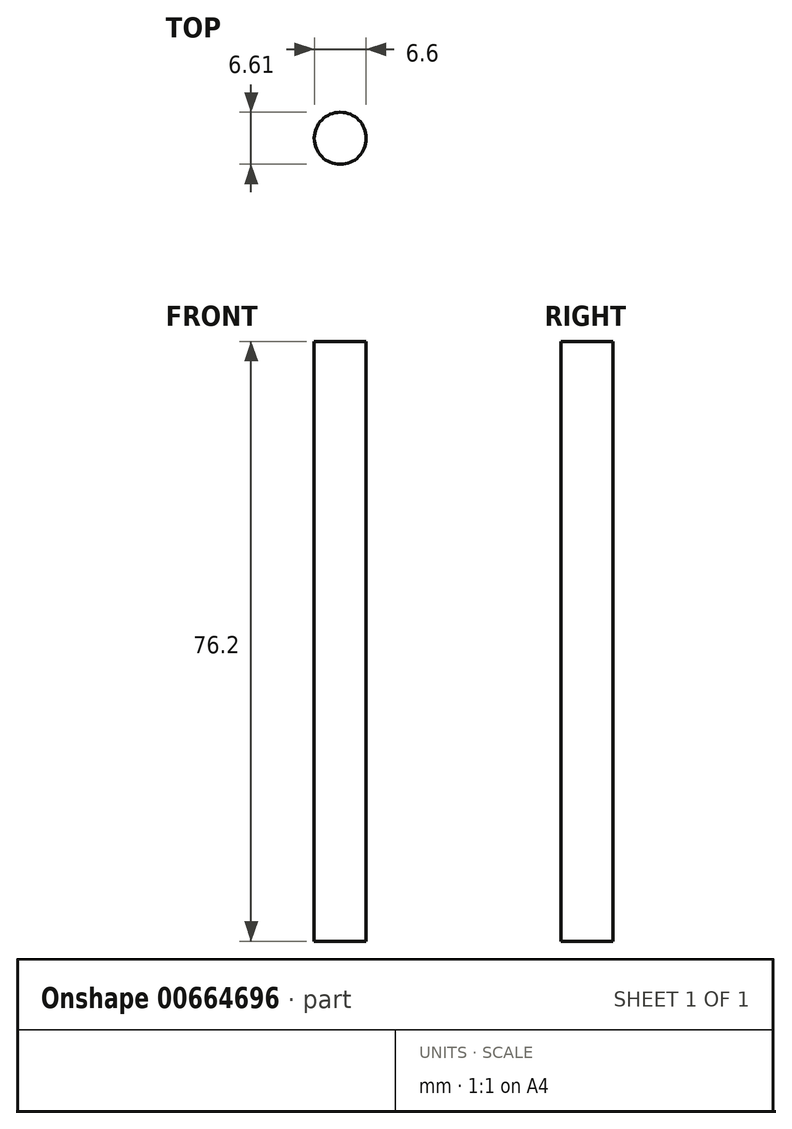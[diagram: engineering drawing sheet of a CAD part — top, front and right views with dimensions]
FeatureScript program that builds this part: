
annotation { "Feature Type Name" : "Feature", "Feature Type Description" : "" }
export const myFeature = defineFeature(function(context is Context, id is Id, definition is map)
    precondition{}
    {
        {
            var Q0;
            Q0=qCreatedBy(makeId("Top.planeOp"),FACE);
            var sketch = newSketch(context, id + "F0", { "sketchPlane" : qUnion([Q0])});
            skCircle(sketch, "E0", {"center": v(-48.26, -61.15) * mm, "radius": 3.3 * mm});
            skSolve(sketch);
        }
        {
            var Q0;
            Q0 = qSketchRegion(id + "F0", true);
            extrude(context, id + "F1", {"entities" : qUnion([Q0]), "depth" : 76.2 * mm, "offsetDistance" : 25.4 * mm});
        }
    });
